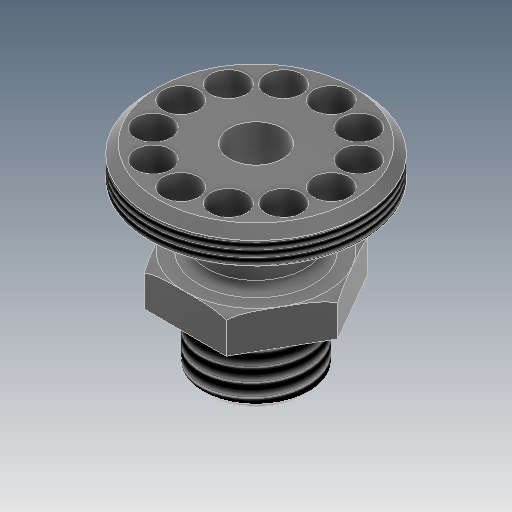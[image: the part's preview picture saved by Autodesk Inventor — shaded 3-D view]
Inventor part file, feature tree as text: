
AUTODESK INVENTOR PART (.ipt)
format: ipt  version: 2025 (Build 290162000, 162)  size: 277,504 bytes
history: native  units: mm
features: sketch x4, extrude x2, thread x2, revolve x1, fillet x1
ambient origin geometry x8: Origin, YZ Plane, XZ Plane, XY Plane, X Axis, Y Axis, Z Axis, Center Point
bodies: 实体1 (feature_tree)
feature tree (10):
  revolve  "旋转1"  [1 undecoded]
  fillet  "圆角1"  Radius=12.0mm
  extrude  "拉伸1"  Depth=24.0mm
  thread  "螺纹1"  [1 undecoded]
  thread  "螺纹2"  [1 undecoded]
  extrude  "拉伸2"  Depth=1.5mm
  sketch  "草图2"  dims[d6=1.0mm d7=18.45mm d8=11.0mm d9=24.0mm]
  sketch  "草图3"  dims[d10=45.0deg d11=1.5mm]
  sketch  "草图4"  dims[d12=2.0mm d13=7.0mm d14=8.0mm d15=22.0mm d16=15.0mm d17=1.5mm d18=360.0deg d19=2.0mm d20=10.0mm d21=0.0mm d22=20.0mm d23=0.0mm d24=20.0mm d25=0.0mm d26=8.0mm d27=17.0mm d28=120.0mm d30=360.0deg d32=10.0mm d33=0.0mm]
  sketch  "草图 - 环形阵列1"  dims[d1=48.0mm d2=12.0mm d3=5.0mm d4=22.0mm d0=6.0mm d5=12.0mm]
note: 3 required parameter values undecoded (feature->parameter linkage not recoverable at this tier; creation-order binding heuristic only, values carry confidence <= 0.55)